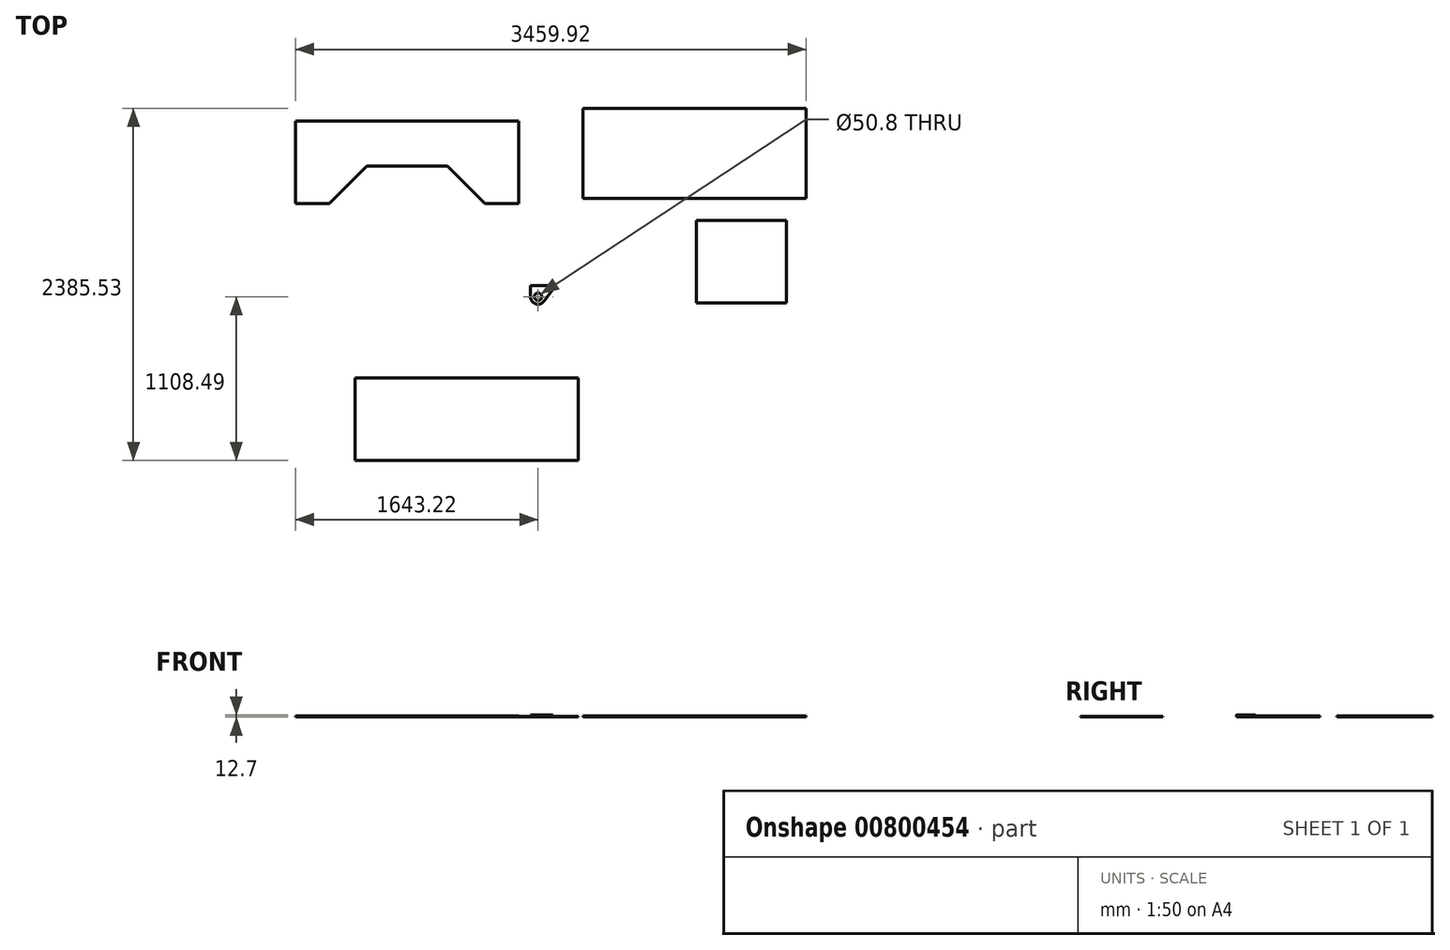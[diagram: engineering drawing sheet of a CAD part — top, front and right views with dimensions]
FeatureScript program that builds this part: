
annotation { "Feature Type Name" : "Feature", "Feature Type Description" : "" }
export const myFeature = defineFeature(function(context is Context, id is Id, definition is map)
    precondition{}
    {
        {
            var Q0;
            Q0=qCreatedBy(makeId("Top.planeOp"),FACE);
            var sketch = newSketch(context, id + "F0", { "sketchPlane" : qUnion([Q0])});
            skLineSegment(sketch, "E0.bottom", {"start": v(-1530.29, 521.5) * mm, "end": v(-18.99, 521.5) * mm});
            skLineSegment(sketch, "E0.top", {"start": v(-1530.29, -37.3) * mm, "end": v(-18.99, -37.3) * mm});
            skLineSegment(sketch, "E0.left", {"start": v(-1530.29, 521.5) * mm, "end": v(-1530.29, -37.3) * mm});
            skLineSegment(sketch, "E0.right", {"start": v(-18.99, 521.5) * mm, "end": v(-18.99, -37.3) * mm});
            skSolve(sketch);
        }
        {
            var Q0;
            Q0 = qSketchRegion(id + "F0", true);
            extrude(context, id + "F1", {"entities" : qUnion([Q0]), "depth" : 6.35 * mm, "offsetDistance" : 25.4 * mm});
        }
        {
            var Q0;
            Q0=qCreatedBy(makeId("Top.planeOp"),FACE);
            var sketch = newSketch(context, id + "F2", { "sketchPlane" : qUnion([Q0])});
            skLineSegment(sketch, "E1.bottom", {"start": v(418.33, 609.6) * mm, "end": v(1929.63, 609.6) * mm});
            skLineSegment(sketch, "E1.top", {"start": v(418.33, 0) * mm, "end": v(1929.63, 0) * mm});
            skLineSegment(sketch, "E1.left", {"start": v(418.33, 609.6) * mm, "end": v(418.33, 0) * mm});
            skLineSegment(sketch, "E1.right", {"start": v(1929.63, 609.6) * mm, "end": v(1929.63, 0) * mm});
            skSolve(sketch);
        }
        {
            var Q0;
            Q0 = qSketchRegion(id + "F2", true);
            extrude(context, id + "F3", {"entities" : qUnion([Q0]), "depth" : 6.35 * mm, "offsetDistance" : 25.4 * mm});
        }
        {
            var Q0;
            Q0=makeQuery(id+"F1.opExtrude","CAP_FACE",FACE,{"disambiguationData":[OSD([sQuery(id+"F0.wireOp",EDGE,"E0.bottom"),sQuery(id+"F0.wireOp",EDGE,"E0.top"),sQuery(id+"F0.wireOp",EDGE,"E0.left"),sQuery(id+"F0.wireOp",EDGE,"E0.right")])],"isStart":true});
            var sketch = newSketch(context, id + "F4", { "sketchPlane" : qUnion([Q0])});
            skLineSegment(sketch, "E2", {"start": v(-1047.69, -216.7) * mm, "end": v(-501.59, -216.7) * mm});
            skLineSegment(sketch, "E3", {"start": v(-501.59, -216.7) * mm, "end": v(-247.59, 37.3) * mm});
            skLineSegment(sketch, "E4", {"start": v(-247.59, 37.3) * mm, "end": v(-1301.69, 37.3) * mm});
            skLineSegment(sketch, "E5", {"start": v(-1301.69, 37.3) * mm, "end": v(-1047.69, -216.7) * mm});
            skSolve(sketch);
        }
        {
            var Q0;
            Q0 = qSketchRegion(id + "F4", true);
            extrude(context, id + "F5", {"entities" : qUnion([Q0]), "operationType" : NewBodyOperationType.REMOVE, "endBound" : BoundingType.THROUGH_ALL, "oppositeDirection" : true, "depth" : 25.4 * mm, "offsetDistance" : 25.4 * mm});
        }
        {
            var Q0;
            Q0 = qSketchRegion(id + "F4", true);
            extrude(context, id + "F6", {"entities" : qUnion([Q0]), "operationType" : NewBodyOperationType.REMOVE, "depth" : 25.4 * mm, "offsetDistance" : 25.4 * mm});
        }
        {
            var Q0;
            Q0=qCreatedBy(makeId("Top.planeOp"),FACE);
            var sketch = newSketch(context, id + "F7", { "sketchPlane" : qUnion([Q0])});
            skLineSegment(sketch, "E6.bottom", {"start": v(1794.52, -150.57) * mm, "end": v(1184.92, -150.57) * mm});
            skLineSegment(sketch, "E6.top", {"start": v(1794.52, -709.37) * mm, "end": v(1184.92, -709.37) * mm});
            skLineSegment(sketch, "E6.left", {"start": v(1794.52, -150.57) * mm, "end": v(1794.52, -709.37) * mm});
            skLineSegment(sketch, "E6.right", {"start": v(1184.92, -150.57) * mm, "end": v(1184.92, -709.37) * mm});
            skSolve(sketch);
        }
        {
            var Q0;
            Q0 = qSketchRegion(id + "F7", true);
            extrude(context, id + "F8", {"entities" : qUnion([Q0]), "depth" : 6.35 * mm, "offsetDistance" : 25.4 * mm});
        }
        {
            var Q0;
            Q0=qCreatedBy(makeId("Top.planeOp"),FACE);
            var sketch = newSketch(context, id + "F9", { "sketchPlane" : qUnion([Q0])});
            skLineSegment(sketch, "E7", {"start": v(214.54, -591.24) * mm, "end": v(62.14, -591.24) * mm});
            skLineSegment(sketch, "E8", {"start": v(62.14, -591.24) * mm, "end": v(62.14, -667.44) * mm});
            skArc(sketch, "E9", {"start": v(62.14, -667.44) * mm, "mid": v(96.87, -715.63) * mm, "end": v(153.58, -697.92) * mm});
            skLineSegment(sketch, "E10", {"start": v(153.58, -697.92) * mm, "end": v(214.54, -616.64) * mm});
            skLineSegment(sketch, "E11", {"start": v(214.54, -616.64) * mm, "end": v(214.54, -591.24) * mm});
            skCircle(sketch, "E12", {"center": v(112.94, -667.44) * mm, "radius": 25.4 * mm});
            skSolve(sketch);
        }
        {
            var Q0;
            Q0 = qSketchRegion(id + "F9", true);
            extrude(context, id + "F10", {"entities" : qUnion([Q0]), "depth" : 12.7 * mm, "offsetDistance" : 25.4 * mm});
        }
        {
            var Q0;
            Q0=qCreatedBy(makeId("Top.planeOp"),FACE);
            var sketch = newSketch(context, id + "F11", { "sketchPlane" : qUnion([Q0])});
            skLineSegment(sketch, "E13.bottom", {"start": v(384.45, -1217.13) * mm, "end": v(-1126.85, -1217.13) * mm});
            skLineSegment(sketch, "E13.top", {"start": v(384.45, -1775.93) * mm, "end": v(-1126.85, -1775.93) * mm});
            skLineSegment(sketch, "E13.left", {"start": v(384.45, -1217.13) * mm, "end": v(384.45, -1775.93) * mm});
            skLineSegment(sketch, "E13.right", {"start": v(-1126.85, -1217.13) * mm, "end": v(-1126.85, -1775.93) * mm});
            skSolve(sketch);
        }
        {
            var Q0;
            Q0 = qSketchRegion(id + "F11", true);
            extrude(context, id + "F12", {"entities" : qUnion([Q0]), "depth" : 4.76 * mm, "offsetDistance" : 25.4 * mm});
        }
    });
